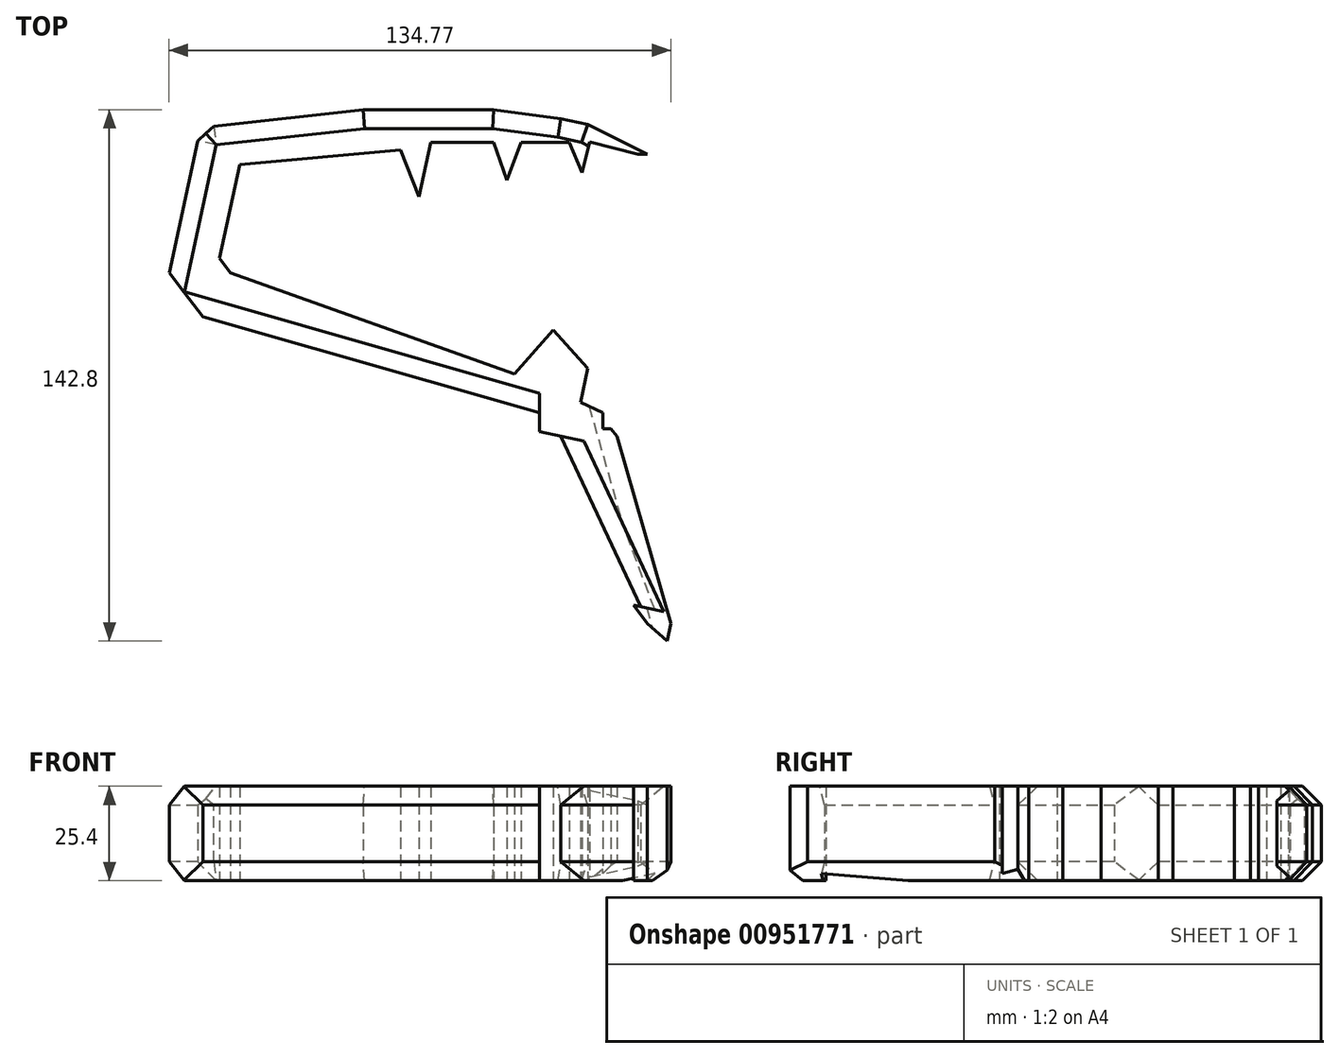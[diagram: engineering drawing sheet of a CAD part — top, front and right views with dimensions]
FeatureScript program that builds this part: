
annotation { "Feature Type Name" : "Feature", "Feature Type Description" : "" }
export const myFeature = defineFeature(function(context is Context, id is Id, definition is map)
    precondition{}
    {
        {
            var Q0;
            Q0=qCreatedBy(makeId("Top.planeOp"),FACE);
            var sketch = newSketch(context, id + "F0", { "sketchPlane" : qUnion([Q0])});
            skLineSegment(sketch, "E0", {"start": v(67.01, 51.9) * mm, "end": v(54.1, 55.21) * mm});
            skLineSegment(sketch, "E1", {"start": v(54.1, 55.21) * mm, "end": v(51.98, 46.94) * mm});
            skLineSegment(sketch, "E2", {"start": v(51.98, 46.94) * mm, "end": v(48.58, 55.03) * mm});
            skLineSegment(sketch, "E3", {"start": v(48.58, 55.03) * mm, "end": v(35.67, 55.03) * mm});
            skLineSegment(sketch, "E4", {"start": v(35.67, 55.03) * mm, "end": v(31.8, 44.9) * mm});
            skLineSegment(sketch, "E5", {"start": v(31.8, 44.9) * mm, "end": v(28.3, 55.03) * mm});
            skLineSegment(sketch, "E6", {"start": v(28.3, 55.03) * mm, "end": v(11.34, 55.03) * mm});
            skLineSegment(sketch, "E7", {"start": v(11.34, 55.03) * mm, "end": v(8.2, 40.47) * mm});
            skLineSegment(sketch, "E8", {"start": v(8.2, 40.47) * mm, "end": v(3.22, 53) * mm});
            skLineSegment(sketch, "E9", {"start": v(3.22, 53) * mm, "end": v(-39.92, 49.13) * mm});
            skLineSegment(sketch, "E10", {"start": v(-39.92, 49.13) * mm, "end": v(-45.32, 24.02) * mm});
            skLineSegment(sketch, "E11", {"start": v(-45.32, 24.02) * mm, "end": v(-42.5, 20) * mm});
            skLineSegment(sketch, "E12", {"start": v(-42.5, 20) * mm, "end": v(33.83, -7.1) * mm});
            skLineSegment(sketch, "E13", {"start": v(33.83, -7.1) * mm, "end": v(44.34, 4.7) * mm});
            skLineSegment(sketch, "E14", {"start": v(44.34, 4.7) * mm, "end": v(53.55, -5.62) * mm});
            skLineSegment(sketch, "E15", {"start": v(53.55, -5.62) * mm, "end": v(51.6, -14.75) * mm});
            skLineSegment(sketch, "E16", {"start": v(51.6, -14.75) * mm, "end": v(57.61, -17.6) * mm});
            skLineSegment(sketch, "E17", {"start": v(57.61, -17.6) * mm, "end": v(57.61, -21.85) * mm});
            skLineSegment(sketch, "E18", {"start": v(57.61, -21.85) * mm, "end": v(59.82, -21.85) * mm});
            skLineSegment(sketch, "E19", {"start": v(59.82, -21.85) * mm, "end": v(61.48, -23.87) * mm});
            skLineSegment(sketch, "E20", {"start": v(61.48, -23.87) * mm, "end": v(75.86, -74.2) * mm});
            skLineSegment(sketch, "E21", {"start": v(75.86, -74.2) * mm, "end": v(74.85, -78.92) * mm});
            skLineSegment(sketch, "E22", {"start": v(74.85, -78.92) * mm, "end": v(69.6, -74.2) * mm});
            skLineSegment(sketch, "E23", {"start": v(69.6, -74.2) * mm, "end": v(65.9, -69.23) * mm});
            skLineSegment(sketch, "E24", {"start": v(65.9, -69.23) * mm, "end": v(67.73, -69.62) * mm});
            skLineSegment(sketch, "E25", {"start": v(67.73, -69.62) * mm, "end": v(46.36, -23.87) * mm});
            skLineSegment(sketch, "E26", {"start": v(46.36, -23.87) * mm, "end": v(40.56, -22.63) * mm});
            skLineSegment(sketch, "E27", {"start": v(40.56, -22.63) * mm, "end": v(40.56, -17.6) * mm});
            skLineSegment(sketch, "E28", {"start": v(40.56, -17.6) * mm, "end": v(-49.87, 8.2) * mm});
            skLineSegment(sketch, "E29", {"start": v(-49.87, 8.2) * mm, "end": v(-58.9, 20) * mm});
            skLineSegment(sketch, "E30", {"start": v(-58.9, 20) * mm, "end": v(-50.5, 59.05) * mm});
            skLineSegment(sketch, "E31", {"start": v(-50.5, 59.05) * mm, "end": v(-6.73, 63.88) * mm});
            skLineSegment(sketch, "E32", {"start": v(-6.73, 63.88) * mm, "end": v(17.97, 63.88) * mm});
            skLineSegment(sketch, "E33", {"start": v(17.97, 63.88) * mm, "end": v(28.3, 63.88) * mm});
            skLineSegment(sketch, "E34", {"start": v(28.3, 63.88) * mm, "end": v(46.36, 61.48) * mm});
            skLineSegment(sketch, "E35", {"start": v(46.36, 61.48) * mm, "end": v(53.55, 59.94) * mm});
            skLineSegment(sketch, "E36", {"start": v(53.55, 59.94) * mm, "end": v(69.6, 51.9) * mm});
            skLineSegment(sketch, "E37", {"start": v(69.6, 51.9) * mm, "end": v(67.01, 51.9) * mm});
            skSolve(sketch);
        }
        {
            var Q0;
            Q0=qCreatedBy(makeId("Top.planeOp"),FACE);
            var sketch = newSketch(context, id + "F1", { "sketchPlane" : qUnion([Q0])});
            skSolve(sketch);
        }
        {
            var Q0;
            Q0 = qSketchRegion(id + "F1", true);
            var Q1;
            Q1=makeQuery(id+"F0.imprint","IMPRINT",FACE,{"disambiguationData":[TD([[makeQuery(id+"F0.imprint","IMPRINT",EDGE,{"derivedFrom":sQuery(id+"F0.wireOp",EDGE,"E0")}),-1.0]])]});
            extrude(context, id + "F2", {"entities" : qUnion([Q0, Q1]), "depth" : 25.4 * mm, "offsetDistance" : 25.4 * mm});
        }
        {
            var Q0;
            Q0=makeQuery(id+"F2.opExtrude","CAP_EDGE",EDGE,{"disambiguationData":[OSD([sQuery(id+"F0.wireOp",EDGE,"E28")])],"isStart":true});
            chamfer(context, id + "F3", {"entities" : qUnion([Q0]), "width" : 5.08 * mm, "tangentPropagation" : true});
        }
        {
            var Q0;
            Q0=makeQuery(id+"F2.opExtrude","CAP_EDGE",EDGE,{"disambiguationData":[OSD([sQuery(id+"F0.wireOp",EDGE,"E28")])],"isStart":false});
            var Q1;
            Q1=makeQuery(id+"F2.opExtrude","CAP_EDGE",EDGE,{"disambiguationData":[OSD([sQuery(id+"F0.wireOp",EDGE,"E20")])],"isStart":true});
            var Q2;
            Q2=makeQuery(id+"F2.opExtrude","CAP_EDGE",EDGE,{"disambiguationData":[OSD([sQuery(id+"F0.wireOp",EDGE,"E25")])],"isStart":true});
            var Q3;
            Q3=makeQuery(id+"F2.opExtrude","CAP_EDGE",EDGE,{"disambiguationData":[OSD([sQuery(id+"F0.wireOp",EDGE,"E30")])],"isStart":true});
            var Q4;
            Q4=makeQuery(id+"F2.opExtrude","SWEPT_EDGE",EDGE,{"disambiguationData":[OSD([sQuery(id+"F0.wireOp",EDGE,"E30"),sQuery(id+"F0.wireOp",EDGE,"E31")])]});
            var Q5;
            Q5=makeQuery(id+"F2.opExtrude","CAP_EDGE",EDGE,{"disambiguationData":[OSD([sQuery(id+"F0.wireOp",EDGE,"E31")])],"isStart":false});
            var Q6;
            Q6=makeQuery(id+"F2.opExtrude","CAP_EDGE",EDGE,{"disambiguationData":[OSD([sQuery(id+"F0.wireOp",EDGE,"E31")])],"isStart":true});
            var Q7;
            Q7=makeQuery(id+"F2.opExtrude","CAP_EDGE",EDGE,{"disambiguationData":[OSD([sQuery(id+"F0.wireOp",EDGE,"E32"),sQuery(id+"F0.wireOp",EDGE,"E33")])],"isStart":true});
            var Q8;
            Q8=makeQuery(id+"F2.opExtrude","CAP_EDGE",EDGE,{"disambiguationData":[OSD([sQuery(id+"F0.wireOp",EDGE,"E32"),sQuery(id+"F0.wireOp",EDGE,"E33")])],"isStart":false});
            var Q9;
            Q9=makeQuery(id+"F2.opExtrude","CAP_EDGE",EDGE,{"disambiguationData":[OSD([sQuery(id+"F0.wireOp",EDGE,"E34")])],"isStart":true});
            var Q10;
            Q10=makeQuery(id+"F2.opExtrude","CAP_EDGE",EDGE,{"disambiguationData":[OSD([sQuery(id+"F0.wireOp",EDGE,"E34")])],"isStart":false});
            var Q11;
            Q11=makeQuery(id+"F2.opExtrude","CAP_EDGE",EDGE,{"disambiguationData":[OSD([sQuery(id+"F0.wireOp",EDGE,"E35")])],"isStart":true});
            var Q12;
            Q12=makeQuery(id+"F2.opExtrude","CAP_EDGE",EDGE,{"disambiguationData":[OSD([sQuery(id+"F0.wireOp",EDGE,"E35")])],"isStart":false});
            var Q13;
            Q13=makeQuery(id+"F2.opExtrude","CAP_EDGE",EDGE,{"disambiguationData":[OSD([sQuery(id+"F0.wireOp",EDGE,"E36")])],"isStart":true});
            var Q14;
            Q14=makeQuery(id+"F2.opExtrude","CAP_EDGE",EDGE,{"disambiguationData":[OSD([sQuery(id+"F0.wireOp",EDGE,"E36")])],"isStart":false});
            var Q15;
            Q15=makeQuery(id+"F2.opExtrude","CAP_EDGE",EDGE,{"disambiguationData":[OSD([sQuery(id+"F0.wireOp",EDGE,"E25")])],"isStart":false});
            chamfer(context, id + "F4", {"entities" : qUnion([Q0, Q1, Q2, Q3, Q4, Q5, Q6, Q7, Q8, Q9, Q10, Q11, Q12, Q13, Q14, Q15]), "width" : 5.08 * mm, "tangentPropagation" : true});
        }
        {
            var Q0;
            Q0=makeQuery(id+"F2.opExtrude","CAP_EDGE",EDGE,{"disambiguationData":[OSD([sQuery(id+"F0.wireOp",EDGE,"E30")])],"isStart":false});
            chamfer(context, id + "F5", {"entities" : qUnion([Q0]), "width" : 5.08 * mm, "tangentPropagation" : true});
        }
    });
